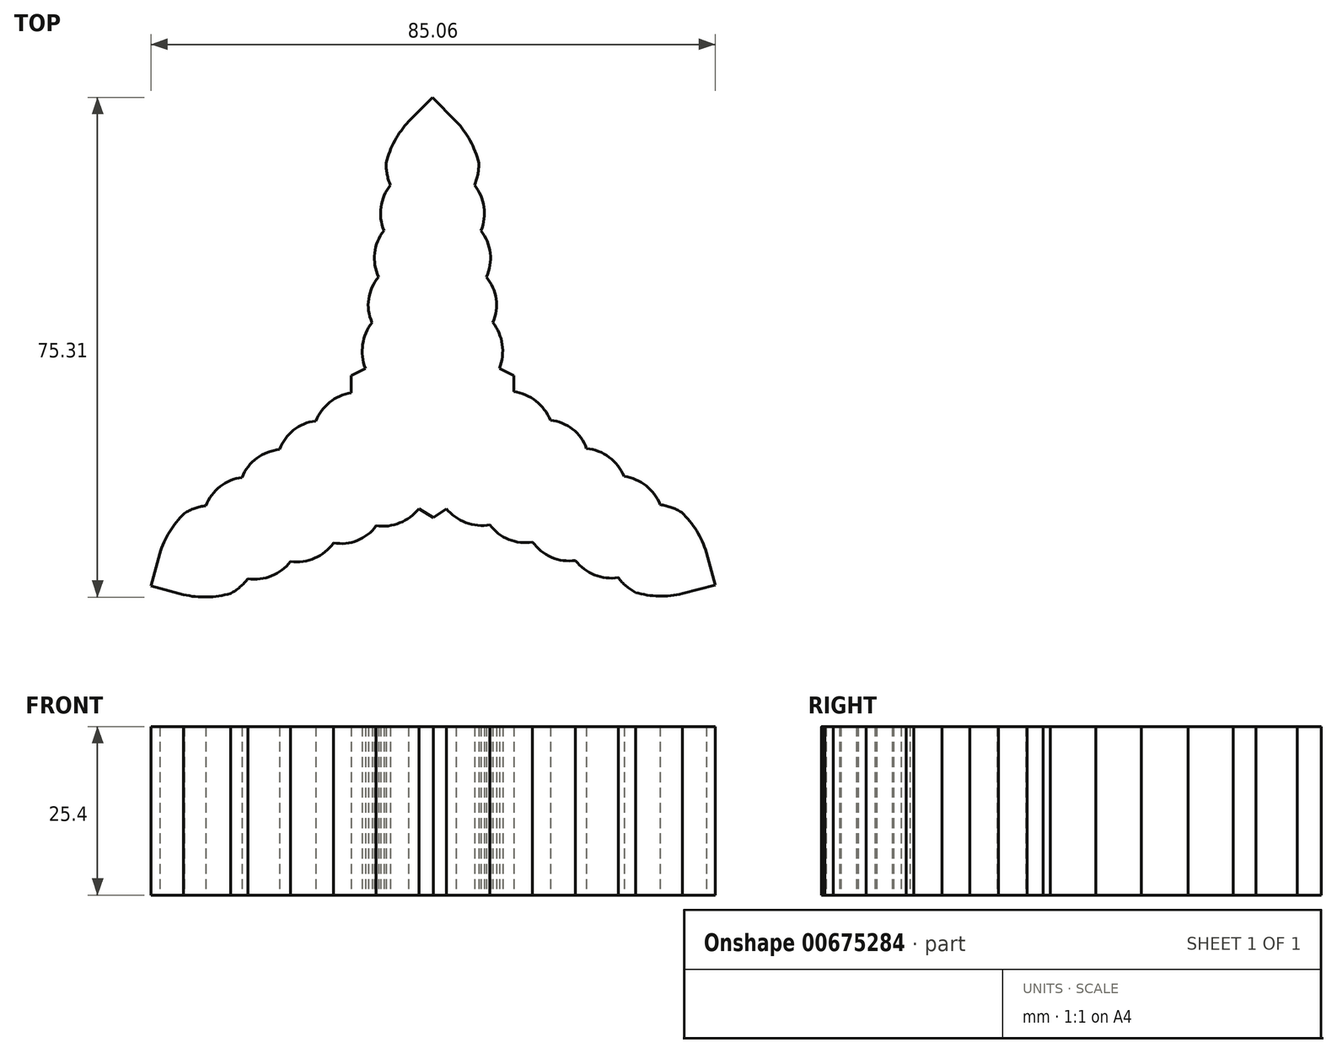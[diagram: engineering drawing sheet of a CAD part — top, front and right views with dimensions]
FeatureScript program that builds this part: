
annotation { "Feature Type Name" : "Feature", "Feature Type Description" : "" }
export const myFeature = defineFeature(function(context is Context, id is Id, definition is map)
    precondition{}
    {
        {
            var Q0;
            Q0=qCreatedBy(makeId("Top.planeOp"),FACE);
            var sketch = newSketch(context, id + "F0", { "sketchPlane" : qUnion([Q0])});
            skPoint(sketch, "E0.center", {"position": v(0, 0) * mm});
            skPoint(sketch, "E1", {"position": v(-0.1, 49.08) * mm});
            skLineSegment(sketch, "E2", {"start": v(-0.1, 49.08) * mm, "end": v(-3.7, 45.45) * mm});
            skArc(sketch, "E3", {"start": v(-3.7, 45.45) * mm, "mid": v(-5.78, 42.54) * mm, "end": v(-7.08, 39.21) * mm});
            skArc(sketch, "E4.trimOffspring", {"start": v(-7.08, 39.21) * mm, "mid": v(-6.95, 37.5) * mm, "end": v(-6.45, 35.84) * mm});
            skLineSegment(sketch, "E5", {"start": v(-0.1, 49.08) * mm, "end": v(-0.1, 48.22) * mm});
            skArc(sketch, "E6", {"start": v(-6.45, 35.84) * mm, "mid": v(-7.87, 32.54) * mm, "end": v(-7.42, 28.98) * mm});
            skArc(sketch, "E7", {"start": v(-7.42, 28.98) * mm, "mid": v(-8.81, 25.6) * mm, "end": v(-8.23, 21.98) * mm});
            skArc(sketch, "E8", {"start": v(-8.23, 21.98) * mm, "mid": v(-9.72, 18.7) * mm, "end": v(-9.2, 15.13) * mm});
            skArc(sketch, "E9", {"start": v(-9.2, 15.13) * mm, "mid": v(-10.62, 11.82) * mm, "end": v(-10.2, 8.25) * mm});
            skLineSegment(sketch, "E10", {"start": v(-10.2, 8.25) * mm, "end": v(-12.37, 7.15) * mm});
            skLineSegment(sketch, "E11", {"start": v(-12.37, 7.15) * mm, "end": v(-12.37, 4.64) * mm});
            skLineSegment(sketch, "E12.MirrorCS", {"start": v(-0.1, 49.08) * mm, "end": v(3.48, 45.45) * mm});
            skArc(sketch, "E13.MirrorCS", {"start": v(3.48, 45.45) * mm, "mid": v(5.57, 42.54) * mm, "end": v(6.86, 39.21) * mm});
            skArc(sketch, "E14.MirrorCS", {"start": v(6.86, 39.21) * mm, "mid": v(6.73, 37.5) * mm, "end": v(6.23, 35.84) * mm});
            skLineSegment(sketch, "E15.MirrorCS", {"start": v(12.16, 7.15) * mm, "end": v(12.16, 4.64) * mm});
            skLineSegment(sketch, "E16.MirrorCS", {"start": v(10, 8.25) * mm, "end": v(12.16, 7.15) * mm});
            skArc(sketch, "E17.MirrorCS", {"start": v(9, 15.13) * mm, "mid": v(10.4, 11.82) * mm, "end": v(10, 8.25) * mm});
            skArc(sketch, "E18.MirrorCS", {"start": v(8.01, 21.98) * mm, "mid": v(9.5, 18.7) * mm, "end": v(9, 15.13) * mm});
            skArc(sketch, "E19.MirrorCS", {"start": v(7.2, 28.98) * mm, "mid": v(8.6, 25.6) * mm, "end": v(8.01, 21.98) * mm});
            skArc(sketch, "E20.MirrorCS", {"start": v(6.23, 35.84) * mm, "mid": v(7.66, 32.54) * mm, "end": v(7.2, 28.98) * mm});
            skLineSegment(sketch, "E21", {"start": v(42.5, -24.43) * mm, "end": v(41.16, -19.51) * mm});
            skArc(sketch, "E22", {"start": v(41.16, -19.51) * mm, "mid": v(39.69, -16.25) * mm, "end": v(37.45, -13.46) * mm});
            skArc(sketch, "E23.trimOffspring", {"start": v(37.45, -13.46) * mm, "mid": v(35.9, -12.71) * mm, "end": v(34.22, -12.32) * mm});
            skArc(sketch, "E24", {"start": v(34.22, -12.32) * mm, "mid": v(32.07, -9.44) * mm, "end": v(28.76, -8.05) * mm});
            skArc(sketch, "E25", {"start": v(28.76, -8.05) * mm, "mid": v(26.53, -5.15) * mm, "end": v(23.1, -3.85) * mm});
            skArc(sketch, "E26", {"start": v(23.1, -3.85) * mm, "mid": v(21, -0.92) * mm, "end": v(17.66, 0.43) * mm});
            skArc(sketch, "E27", {"start": v(17.66, 0.43) * mm, "mid": v(15.48, 3.32) * mm, "end": v(12.16, 4.74) * mm});
            skLineSegment(sketch, "E28.MirrorCS", {"start": v(42.5, -24.43) * mm, "end": v(37.57, -25.72) * mm});
            skArc(sketch, "E29.MirrorCS", {"start": v(37.57, -25.72) * mm, "mid": v(34.01, -26.08) * mm, "end": v(30.48, -25.53) * mm});
            skArc(sketch, "E30.MirrorCS", {"start": v(30.48, -25.53) * mm, "mid": v(29.06, -24.56) * mm, "end": v(27.87, -23.3) * mm});
            skArc(sketch, "E31.MirrorCS", {"start": v(8.56, -15.34) * mm, "mid": v(4.94, -15) * mm, "end": v(1.97, -12.9) * mm});
            skArc(sketch, "E32.MirrorCS", {"start": v(14.98, -17.91) * mm, "mid": v(11.4, -17.56) * mm, "end": v(8.56, -15.34) * mm});
            skArc(sketch, "E33.MirrorCS", {"start": v(21.45, -20.71) * mm, "mid": v(17.82, -20.23) * mm, "end": v(14.98, -17.91) * mm});
            skArc(sketch, "E34.MirrorCS", {"start": v(27.87, -23.3) * mm, "mid": v(24.3, -22.89) * mm, "end": v(21.45, -20.71) * mm});
            skLineSegment(sketch, "E35", {"start": v(1.97, -12.9) * mm, "end": v(0, -14.26) * mm});
            skLineSegment(sketch, "E36", {"start": v(0, -14.26) * mm, "end": v(-2.14, -12.9) * mm});
            skLineSegment(sketch, "E37", {"start": v(-42.55, -24.57) * mm, "end": v(-37.61, -25.86) * mm});
            skArc(sketch, "E38", {"start": v(-37.61, -25.86) * mm, "mid": v(-34.05, -26.22) * mm, "end": v(-30.52, -25.68) * mm});
            skArc(sketch, "E39.trimOffspring", {"start": v(-30.52, -25.68) * mm, "mid": v(-29.1, -24.7) * mm, "end": v(-27.91, -23.45) * mm});
            skArc(sketch, "E40", {"start": v(-27.91, -23.45) * mm, "mid": v(-24.35, -23.03) * mm, "end": v(-21.5, -20.86) * mm});
            skArc(sketch, "E41", {"start": v(-21.5, -20.86) * mm, "mid": v(-17.86, -20.37) * mm, "end": v(-15.02, -18.05) * mm});
            skArc(sketch, "E42", {"start": v(-15.02, -18.05) * mm, "mid": v(-11.43, -17.7) * mm, "end": v(-8.6, -15.48) * mm});
            skArc(sketch, "E43", {"start": v(-8.6, -15.48) * mm, "mid": v(-5.03, -15.05) * mm, "end": v(-2.14, -12.9) * mm});
            skLineSegment(sketch, "E44.MirrorCS", {"start": v(-42.55, -24.57) * mm, "end": v(-41.2, -19.65) * mm});
            skArc(sketch, "E45.MirrorCS", {"start": v(-41.2, -19.65) * mm, "mid": v(-39.73, -16.4) * mm, "end": v(-37.49, -13.6) * mm});
            skArc(sketch, "E46.MirrorCS", {"start": v(-37.49, -13.6) * mm, "mid": v(-35.93, -12.86) * mm, "end": v(-34.25, -12.46) * mm});
            skArc(sketch, "E47.MirrorCS", {"start": v(-17.7, 0.28) * mm, "mid": v(-15.6, 3.12) * mm, "end": v(-12.37, 4.57) * mm});
            skArc(sketch, "E48.MirrorCS", {"start": v(-23.14, -4) * mm, "mid": v(-21.05, -1.06) * mm, "end": v(-17.7, 0.28) * mm});
            skArc(sketch, "E49.MirrorCS", {"start": v(-28.8, -8.2) * mm, "mid": v(-26.56, -5.3) * mm, "end": v(-23.14, -4) * mm});
            skArc(sketch, "E50.MirrorCS", {"start": v(-34.25, -12.46) * mm, "mid": v(-32.11, -9.58) * mm, "end": v(-28.8, -8.2) * mm});
            skLineSegment(sketch, "E51", {"start": v(-12.37, 4.64) * mm, "end": v(-12.37, 4.57) * mm});
            skSolve(sketch);
        }
        {
            var Q0;
            Q0=makeQuery(id+"F0.imprint","IMPRINT",FACE,{"disambiguationData":[TD([[makeQuery(id+"F0.imprint","IMPRINT",EDGE,{"derivedFrom":sQuery(id+"F0.wireOp",EDGE,"E2")}),1.0]])]});
            extrude(context, id + "F1", {"entities" : qUnion([Q0]), "depth" : 25.4 * mm, "offsetDistance" : 25.4 * mm});
        }
    });
